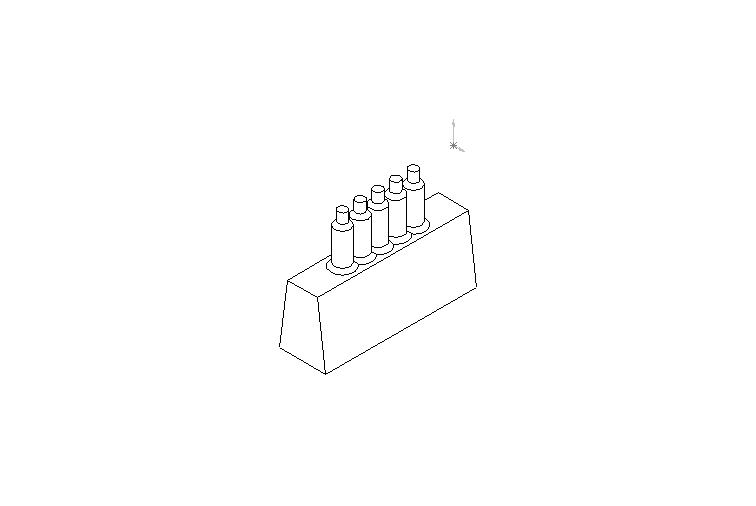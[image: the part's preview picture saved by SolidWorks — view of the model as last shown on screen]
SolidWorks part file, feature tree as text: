
SOLIDWORKS PART (.sldprt)
format: sldprt  version: not decoded by parser v0  size: 150,016 bytes
history: native  units: mm
features: sketch x4, plane x3, extrude x3, pattern_linear x1, fillet x1 + 1 further entry (+2 scaffold rows collapsed)
feature tree (15):
  plane  "Plane1"
  plane  "Plane2"
  plane  "Plane3"
  scaffold x2  (default folders/planes/origin — collapsed)
  sketch  "Sketch1"  dims[c1.D1=7.5mm c1.D2=7.5mm c1.D3=7.5mm c2.D3=15.0deg c2.D4=1.0mm c2.D5=1.0mm c3.D5=97.5deg c4.D5=5.5mm c4.D6=7.0mm c4.D7=1.0mm c5.D7=97.5deg c5.D4=5.5mm]
  sketch  "Sketch2"  dims[c1.D1=1.0mm c1.D2=5.5mm c1.D3=~1.211482mm c1.D4=7.0mm c1.D5=30.0mm c2.D5=82.5deg c2.D1=~3.422965mm c2.D2=7.0mm c2.D3=5.5mm]
  extrude  "Base-Extrude"  Depth=17mm
  sketch  "Sketch3"  dims[D1=1.0mm D2=2.0mm D3=2.0mm D4=2.0mm D5=2.0mm D6=4.5mm]
  extrude  "Boss-Extrude1"  Depth=5.5mm
  sketch  "Sketch4"  dims[D1=1.75mm]
  extrude  "Boss-Extrude2"  Depth=4mm
  pattern_linear  "LPattern1"  Count1=5 Count2=1 Spacing1=2mm Spacing2=50mm
  fillet  "Fillet1"  Radius=0.4mm
  "Annotations"  RD1=7mm RD2=17mm RD3=5.5mm RD4=1mm RD5=1.75mm RD6=2mm
decode coverage: 9 of 9 modeling features carry decoded parameters; 1 rows unclassified (native names shown)
note: ~ marks probable driven/reference dimensions
note: suppression state not decoded; provenance and decode notes live in map.json
